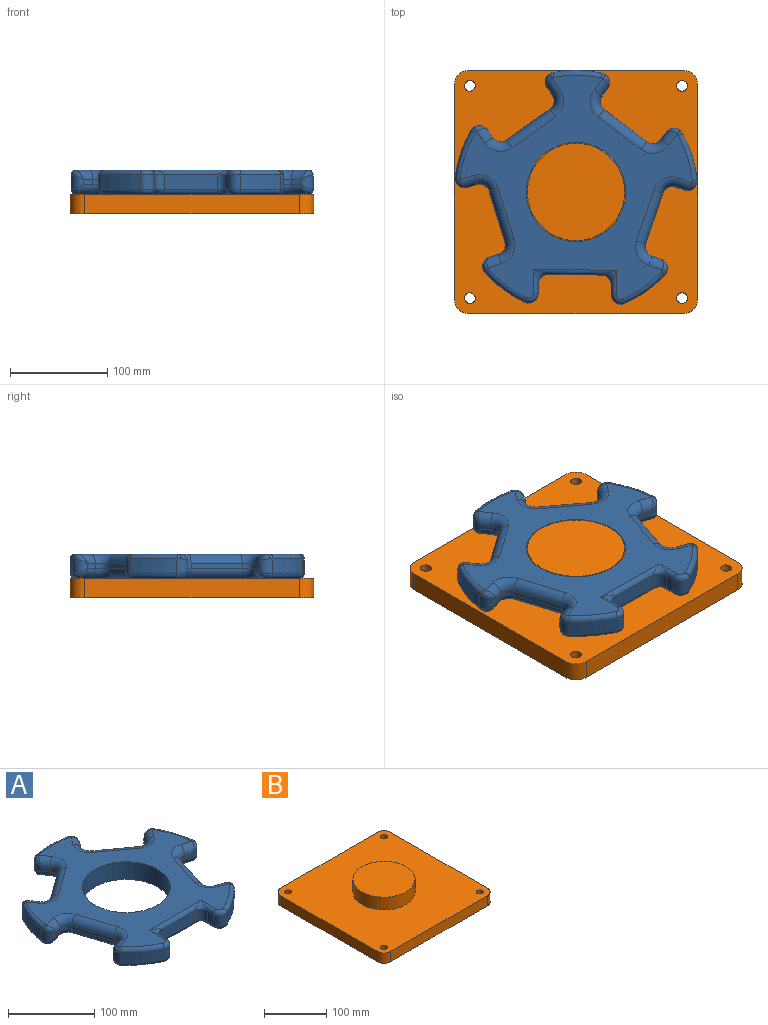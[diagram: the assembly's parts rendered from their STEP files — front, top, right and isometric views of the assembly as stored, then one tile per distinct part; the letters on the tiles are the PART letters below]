
ASSEMBLY  parts=2 mates=1
PART A: 139 faces, bbox 268.9x258.5x25 mm
  f0: cylinder r=125mm len=47.82mm, axis (0,0,-1), area 759.5mm2, adj f3,f5,f97,f126
  f1: plane 238.57x229.73mm, normal (0,0,-1), area 18663.3mm2, adj f3,f4,f7,f10,f13,f15,f20,f21
  f2: plane 238.57x229.73mm, normal (0,0,1), area 18663.3mm2, adj f5,f8,f11,f14,f15,f23,f24,f25
  f3: torus R=120mm, axis (0,0,1), area 391.9mm2, adj f0,f1,f96,f127
  f4: torus R=120mm, axis (0,0,1), area 391.9mm2, adj f1,f16,f27,f121
  f5: torus R=120mm, axis (0,0,1), area 391.9mm2, adj f0,f2,f92,f120
  f6: cylinder r=125mm len=50.29mm, axis (0,0,-1), area 759.5mm2, adj f7,f8,f72,f101
  f7: torus R=120mm, axis (0,0,1), area 391.9mm2, adj f1,f6,f71,f102
  f8: torus R=120mm, axis (0,0,1), area 391.9mm2, adj f2,f6,f67,f95
  f9: cylinder r=125mm len=47.82mm, axis (0,0,-1), area 759.5mm2, adj f10,f11,f47,f76
  f10: torus R=120mm, axis (0,0,1), area 391.9mm2, adj f1,f9,f46,f77
  f11: torus R=120mm, axis (0,0,1), area 391.9mm2, adj f2,f9,f42,f70
  f12: cylinder r=125mm len=40.68mm, axis (0,0,-1), area 759.5mm2, adj f13,f14,f31,f51
  f13: torus R=120mm, axis (0,0,1), area 391.9mm2, adj f1,f12,f30,f52
  f14: torus R=120mm, axis (0,0,1), area 391.9mm2, adj f2,f12,f32,f45
  f15: cylinder r=51mm len=102mm, axis (0,0,-1), area 8011.1mm2, adj f1,f2
  f16: cylinder r=125mm len=40.68mm, axis (0,0,-1), area 759.5mm2, adj f4,f24,f28,f122
  f17: plane 15x9.73mm, normal (-1,0,0), area 146mm2, adj f22,f23,f28,f37
  f18: plane 55x15mm, normal (0,-1,0), area 825mm2, adj f21,f25,f34,f37
  f19: plane 15x9.73mm, normal (1,0,0), area 146mm2, adj f20,f26,f31,f34
  f20: cylinder r=5mm len=24.73mm, axis (0,-1,0), area 119.2mm2, adj f1,f19,f30,f35
  f21: cylinder r=5mm len=85mm, axis (-1,0,0), area 517.6mm2, adj f1,f18,f35,f38
  f22: cylinder r=5mm len=24.73mm, axis (0,1,0), area 119.2mm2, adj f1,f17,f27,f38
  f23: cylinder r=5mm len=24.73mm, axis (0,-1,0), area 119.2mm2, adj f2,f17,f29,f36
  f24: torus R=120mm, axis (0,0,1), area 391.9mm2, adj f2,f16,f29,f117
  f25: cylinder r=5mm len=85mm, axis (1,0,0), area 517.6mm2, adj f2,f18,f33,f36
  f26: cylinder r=5mm len=24.73mm, axis (0,1,0), area 119.2mm2, adj f2,f19,f32,f33
  f27: torus R=5mm, axis (0,0,1), area 128.3mm2, adj f1,f4,f22,f28
  f28: cylinder r=10mm len=15mm, axis (0,0,-1), area 299.5mm2, adj f16,f17,f27,f29
  f29: torus R=5mm, axis (0,0,1), area 128.3mm2, adj f2,f23,f24,f28
  f30: torus R=5mm, axis (0,0,1), area 128.3mm2, adj f1,f13,f20,f31
  f31: cylinder r=10mm len=15mm, axis (0,0,-1), area 299.5mm2, adj f12,f19,f30,f32
  f32: torus R=5mm, axis (0,0,1), area 128.3mm2, adj f2,f14,f26,f31
  f33: bspline ~15x15mm, area 102.4mm2, adj f25,f26,f34
  f34: cylinder r=10mm len=15mm, axis (0,0,-1), area 235.6mm2, adj f18,f19,f33,f35
  f35: bspline ~15x15mm, area 102.4mm2, adj f20,f21,f34
  f36: bspline ~15x15mm, area 102.4mm2, adj f23,f25,f37
  f37: cylinder r=10mm len=15mm, axis (0,0,-1), area 235.6mm2, adj f17,f18,f36,f38
  f38: bspline ~15x15mm, area 102.4mm2, adj f21,f22,f37
  f39: plane 52.31x17mm, normal (-0.95,-0.31,0), area 275mm2, adj f49,f58,f59,f63
  f40: plane 9.26x5mm, normal (-0.31,0.95,0), area 48.7mm2, adj f50,f51,f59,f60
  f41: plane 9.26x5mm, normal (0.31,-0.95,0), area 48.7mm2, adj f47,f48,f57,f58
  f42: torus R=5mm, axis (0,0,1), area 27.4mm2, adj f2,f11,f43,f47
  f43: bspline ~12.75x10mm, area 82.5mm2, adj f42,f47,f48
  f44: bspline ~12.6x10mm, area 82.5mm2, adj f45,f50,f51
  f45: torus R=5mm, axis (0,0,1), area 27.4mm2, adj f2,f14,f44,f51
  f46: torus R=5mm, axis (0,0,1), area 27.4mm2, adj f1,f10,f47,f53
  f47: cylinder r=10mm len=15mm, axis (0,0,-1), area 242.4mm2, adj f9,f41,f42,f43,f46,f53
  f48: cylinder r=10mm len=17.1mm, axis (0.95,0.31,0), area 202.9mm2, adj f2,f41,f43,f54
  f49: cylinder r=10mm len=55.4mm, axis (0.31,-0.95,0), area 863.9mm2, adj f2,f39,f54,f55
  f50: cylinder r=10mm len=17.1mm, axis (-0.95,-0.31,0), area 202.9mm2, adj f2,f40,f44,f55
  f51: cylinder r=10mm len=16.25mm, axis (0,0,-1), area 242.4mm2, adj f12,f40,f44,f45,f52,f56
  f52: torus R=5mm, axis (0,0,1), area 27.4mm2, adj f1,f13,f51,f56
  f53: bspline ~13.05x10mm, area 82.5mm2, adj f46,f47,f57
  f54: torus R=20mm, axis (0,0,1), area 336.4mm2, adj f2,f48,f49,f58
  f55: torus R=20mm, axis (0,0,1), area 336.4mm2, adj f2,f49,f50,f59
  f56: bspline ~12.6x10mm, area 82.5mm2, adj f51,f52,f60
  f57: cylinder r=10mm len=17.1mm, axis (-0.95,-0.31,0), area 202.9mm2, adj f1,f41,f53,f61
  f58: cylinder r=10mm len=12.6mm, axis (0,0,-1), area 78.5mm2, adj f39,f41,f54,f61
  f59: cylinder r=10mm len=12.6mm, axis (0,0,-1), area 78.5mm2, adj f39,f40,f55,f62
  f60: cylinder r=10mm len=17.1mm, axis (0.95,0.31,0), area 202.9mm2, adj f1,f40,f56,f62
  f61: torus R=20mm, axis (0,0,1), area 336.4mm2, adj f1,f57,f58,f63
  f62: torus R=20mm, axis (0,0,1), area 336.4mm2, adj f1,f59,f60,f63
  f63: cylinder r=10mm len=55.4mm, axis (-0.31,0.95,0), area 863.9mm2, adj f1,f39,f61,f62
  f64: plane 44.5x32.33mm, normal (-0.59,0.81,0), area 275mm2, adj f74,f83,f84,f88
  f65: plane 7.87x5.72mm, normal (0.81,0.59,0), area 48.7mm2, adj f75,f76,f84,f85
  f66: plane 7.87x5.72mm, normal (-0.81,-0.59,0), area 48.7mm2, adj f72,f73,f82,f83
  f67: torus R=5mm, axis (0,0,1), area 27.4mm2, adj f2,f8,f68,f72
  f68: bspline ~14.98x10mm, area 82.5mm2, adj f67,f72,f73
  f69: bspline ~15.45x10mm, area 82.5mm2, adj f70,f75,f76
  f70: torus R=5mm, axis (0,0,1), area 27.4mm2, adj f2,f11,f69,f76
  f71: torus R=5mm, axis (0,0,1), area 27.4mm2, adj f1,f7,f72,f78
  f72: cylinder r=10mm len=15.67mm, axis (0,0,-1), area 242.4mm2, adj f6,f66,f67,f68,f71,f78
  f73: cylinder r=10mm len=17.8mm, axis (0.59,-0.81,0), area 202.9mm2, adj f2,f66,f68,f79
  f74: cylinder r=10mm len=50.37mm, axis (-0.81,-0.59,0), area 863.9mm2, adj f2,f64,f79,f80
  f75: cylinder r=10mm len=17.8mm, axis (-0.59,0.81,0), area 202.9mm2, adj f2,f65,f69,f80
  f76: cylinder r=10mm len=16.78mm, axis (0,0,-1), area 242.4mm2, adj f9,f65,f69,f70,f77,f81
  f77: torus R=5mm, axis (0,0,1), area 27.4mm2, adj f1,f10,f76,f81
  f78: bspline ~14.98x10mm, area 82.5mm2, adj f71,f72,f82
  f79: torus R=20mm, axis (0,0,1), area 336.4mm2, adj f2,f73,f74,f83
  f80: torus R=20mm, axis (0,0,1), area 336.4mm2, adj f2,f74,f75,f84
  f81: bspline ~15.45x10mm, area 82.5mm2, adj f76,f77,f85
  f82: cylinder r=10mm len=17.8mm, axis (-0.59,0.81,0), area 202.9mm2, adj f1,f66,f78,f86
  f83: cylinder r=10mm len=13.97mm, axis (0,0,-1), area 78.5mm2, adj f64,f66,f79,f86
  f84: cylinder r=10mm len=13.97mm, axis (0,0,-1), area 78.5mm2, adj f64,f65,f80,f87
  f85: cylinder r=10mm len=17.8mm, axis (0.59,-0.81,0), area 202.9mm2, adj f1,f65,f81,f87
  f86: torus R=20mm, axis (0,0,1), area 336.4mm2, adj f1,f82,f83,f88
  f87: torus R=20mm, axis (0,0,1), area 336.4mm2, adj f1,f84,f85,f88
  f88: cylinder r=10mm len=50.37mm, axis (0.81,0.59,0), area 863.9mm2, adj f1,f64,f86,f87
  f89: plane 44.5x32.33mm, normal (0.59,0.81,0), area 275mm2, adj f99,f108,f109,f113
  f90: plane 7.87x5.72mm, normal (0.81,-0.59,0), area 48.7mm2, adj f100,f101,f109,f110
  f91: plane 7.87x5.72mm, normal (-0.81,0.59,0), area 48.7mm2, adj f97,f98,f107,f108
  f92: torus R=5mm, axis (0,0,1), area 27.4mm2, adj f2,f5,f93,f97
  f93: bspline ~14.37x10mm, area 82.5mm2, adj f92,f97,f98
  f94: bspline ~14.98x10mm, area 82.5mm2, adj f95,f100,f101
  f95: torus R=5mm, axis (0,0,1), area 27.4mm2, adj f2,f8,f94,f101
  f96: torus R=5mm, axis (0,0,1), area 27.4mm2, adj f1,f3,f97,f103
  f97: cylinder r=10mm len=16.78mm, axis (0,0,-1), area 242.4mm2, adj f0,f91,f92,f93,f96,f103
  f98: cylinder r=10mm len=17.8mm, axis (-0.59,-0.81,0), area 202.9mm2, adj f2,f91,f93,f104
  f99: cylinder r=10mm len=50.37mm, axis (-0.81,0.59,0), area 863.9mm2, adj f2,f89,f104,f105
  f100: cylinder r=10mm len=17.8mm, axis (0.59,0.81,0), area 202.9mm2, adj f2,f90,f94,f105
  f101: cylinder r=10mm len=15.67mm, axis (0,0,-1), area 242.4mm2, adj f6,f90,f94,f95,f102,f106
  f102: torus R=5mm, axis (0,0,1), area 27.4mm2, adj f1,f7,f101,f106
  f103: bspline ~15.45x10mm, area 82.5mm2, adj f96,f97,f107
  f104: torus R=20mm, axis (0,0,1), area 336.4mm2, adj f2,f98,f99,f108
  f105: torus R=20mm, axis (0,0,1), area 336.4mm2, adj f2,f99,f100,f109
  f106: bspline ~14.98x10mm, area 82.5mm2, adj f101,f102,f110
  f107: cylinder r=10mm len=17.8mm, axis (0.59,0.81,0), area 202.9mm2, adj f1,f91,f103,f111
  f108: cylinder r=10mm len=13.97mm, axis (0,0,-1), area 78.5mm2, adj f89,f91,f104,f111
  f109: cylinder r=10mm len=13.97mm, axis (0,0,-1), area 78.5mm2, adj f89,f90,f105,f112
  f110: cylinder r=10mm len=17.8mm, axis (-0.59,-0.81,0), area 202.9mm2, adj f1,f90,f106,f112
  f111: torus R=20mm, axis (0,0,1), area 336.4mm2, adj f1,f107,f108,f113
  f112: torus R=20mm, axis (0,0,1), area 336.4mm2, adj f1,f109,f110,f113
  f113: cylinder r=10mm len=50.37mm, axis (0.81,-0.59,0), area 863.9mm2, adj f1,f89,f111,f112
  f114: plane 52.31x17mm, normal (0.95,-0.31,0), area 275mm2, adj f124,f133,f134,f138
  f115: plane 9.26x5mm, normal (-0.31,-0.95,0), area 48.7mm2, adj f125,f126,f134,f135
  f116: plane 9.26x5mm, normal (0.31,0.95,0), area 48.7mm2, adj f122,f123,f132,f133
  f117: torus R=5mm, axis (0,0,1), area 27.4mm2, adj f2,f24,f118,f122
  f118: bspline ~14.4x10mm, area 82.5mm2, adj f117,f122,f123
  f119: bspline ~13.05x10mm, area 82.5mm2, adj f120,f125,f126
  f120: torus R=5mm, axis (0,0,1), area 27.4mm2, adj f2,f5,f119,f126
  f121: torus R=5mm, axis (0,0,1), area 27.4mm2, adj f1,f4,f122,f128
  f122: cylinder r=10mm len=16.25mm, axis (0,0,-1), area 242.4mm2, adj f16,f116,f117,f118,f121,f128
  f123: cylinder r=10mm len=17.1mm, axis (-0.95,0.31,0), area 202.9mm2, adj f2,f116,f118,f129
  f124: cylinder r=10mm len=55.4mm, axis (0.31,0.95,0), area 863.9mm2, adj f2,f114,f129,f130
  f125: cylinder r=10mm len=17.1mm, axis (0.95,-0.31,0), area 202.9mm2, adj f2,f115,f119,f130
  f126: cylinder r=10mm len=15mm, axis (0,0,-1), area 242.4mm2, adj f0,f115,f119,f120,f127,f131
  f127: torus R=5mm, axis (0,0,1), area 27.4mm2, adj f1,f3,f126,f131
  f128: bspline ~12.6x10mm, area 82.5mm2, adj f121,f122,f132
  f129: torus R=20mm, axis (0,0,1), area 336.4mm2, adj f2,f123,f124,f133
  f130: torus R=20mm, axis (0,0,1), area 336.4mm2, adj f2,f124,f125,f134
  f131: bspline ~13.05x10mm, area 82.5mm2, adj f126,f127,f135
  f132: cylinder r=10mm len=17.1mm, axis (0.95,-0.31,0), area 202.9mm2, adj f1,f116,f128,f136
  f133: cylinder r=10mm len=12.6mm, axis (0,0,-1), area 78.5mm2, adj f114,f116,f129,f136
  f134: cylinder r=10mm len=12.6mm, axis (0,0,-1), area 78.5mm2, adj f114,f115,f130,f137
  f135: cylinder r=10mm len=17.1mm, axis (-0.95,0.31,0), area 202.9mm2, adj f1,f115,f131,f137
  f136: torus R=20mm, axis (0,0,1), area 336.4mm2, adj f1,f132,f133,f138
  f137: torus R=20mm, axis (0,0,1), area 336.4mm2, adj f1,f134,f135,f138
  f138: cylinder r=10mm len=55.4mm, axis (-0.31,-0.95,0), area 863.9mm2, adj f1,f114,f136,f137
PART B: 16 faces, bbox 250x250x45 mm
  f0: plane 220x20mm, normal (1,0,0), area 4400mm2, adj f4,f5,f8,f11
  f1: plane 220x20mm, normal (0,1,0), area 4400mm2, adj f4,f5,f8,f9
  f2: plane 220x20mm, normal (-1,0,0), area 4400mm2, adj f4,f5,f9,f10
  f3: plane 220x20mm, normal (0,-1,0), area 4400mm2, adj f4,f5,f10,f11
  f4: plane 250x250mm, normal (0,0,1), area 54072.7mm2, adj f0,f1,f2,f3,f6,f8,f9,f10
  f5: plane 250x250mm, normal (0,0,-1), area 61926.7mm2, adj f0,f1,f2,f3,f8,f9,f10,f11
  f6: cylinder r=50mm len=100mm, axis (0,0,-1), area 7854mm2, adj f4,f7
  f7: plane 100x100mm, normal (0,0,1), area 7854mm2, adj f6
  f8: cylinder r=15mm len=20mm, axis (0,0,-1), area 471.2mm2, adj f0,f1,f4,f5
  f9: cylinder r=15mm len=20mm, axis (0,0,1), area 471.2mm2, adj f1,f2,f4,f5
  f10: cylinder r=15mm len=20mm, axis (0,0,-1), area 471.2mm2, adj f2,f3,f4,f5
  f11: cylinder r=15mm len=20mm, axis (0,0,1), area 471.2mm2, adj f0,f3,f4,f5
  f12: cylinder r=5.5mm len=20mm, axis (0,0,1), area 691.2mm2, adj f4,f5
  f13: cylinder r=5.5mm len=20mm, axis (0,0,1), area 691.2mm2, adj f4,f5
  f14: cylinder r=5.5mm len=20mm, axis (0,0,1), area 691.2mm2, adj f4,f5
  f15: cylinder r=5.5mm len=20mm, axis (0,0,1), area 691.2mm2, adj f4,f5
PLACE A rot(axis=(0,0,-1),0.7deg) t=(0,0,0)mm
PLACE B at identity fixed
MATE revolute B.f6 <-> A.f0  axis (0,0,1) through (0,0,45)mm
